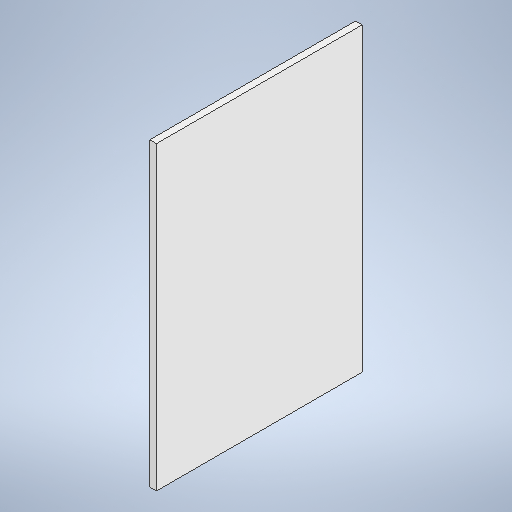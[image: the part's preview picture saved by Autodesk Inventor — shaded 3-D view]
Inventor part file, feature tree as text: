
AUTODESK INVENTOR PART (.ipt)
format: ipt  version: 2025 (Build 290162000, 162)  size: 236,032 bytes
history: native  units: in
note: dims shown in document units (in); Inventor stores cm internally (conversion verified against a paired STEP export)
features: extrude x1, sketch x1
ambient origin geometry x8: Origin, YZ Plane, XZ Plane, XY Plane, X Axis, Y Axis, Z Axis, Center Point
bodies: Solid1 (feature_tree)
feature tree (2):
  extrude  "Extrusion1"  Depth=23.25in
  sketch  "Sketch1"  dims[d1=34.0in d2=23.25in d3=0.75in d4=0.0in]
